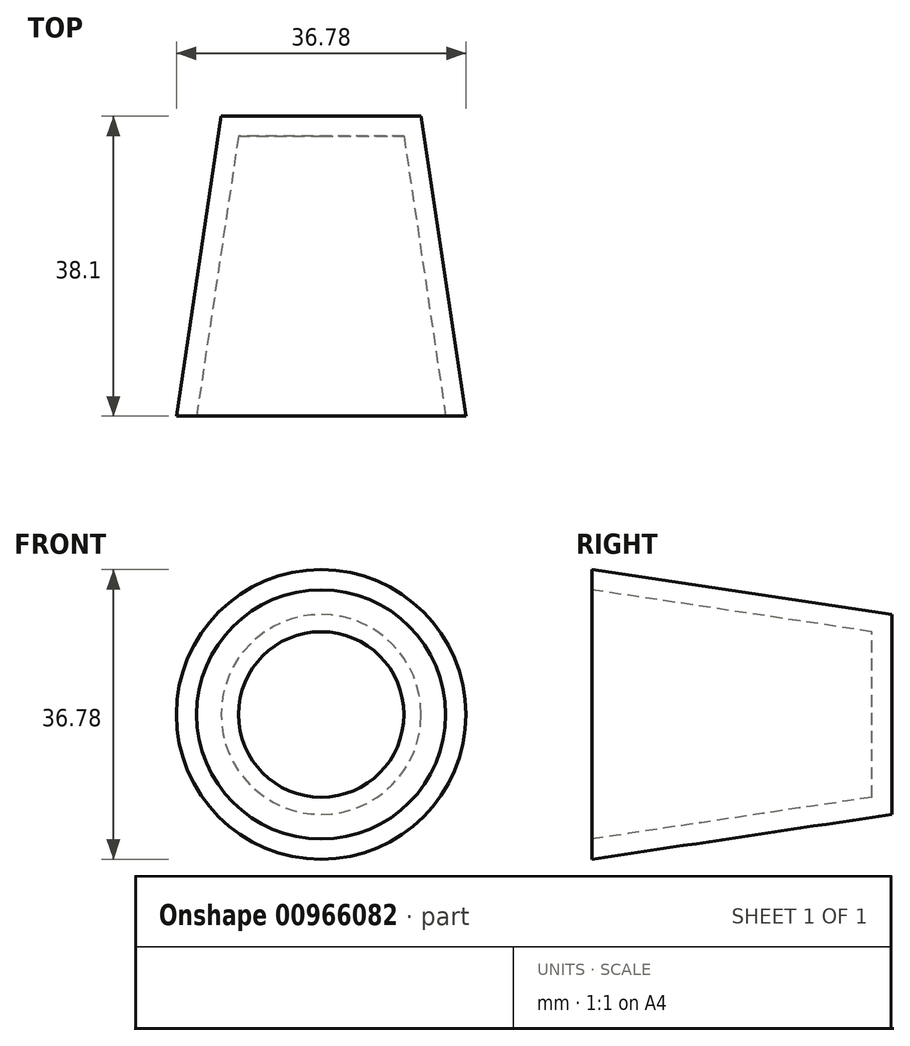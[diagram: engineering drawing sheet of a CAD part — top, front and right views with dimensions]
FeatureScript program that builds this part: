
annotation { "Feature Type Name" : "Feature", "Feature Type Description" : "" }
export const myFeature = defineFeature(function(context is Context, id is Id, definition is map)
    precondition{}
    {
        {
            var Q0;
            Q0=qCreatedBy(makeId("Front.planeOp"),FACE);
            var sketch = newSketch(context, id + "F0", { "sketchPlane" : qUnion([Q0])});
            skCircle(sketch, "E0", {"center": v(0, 0) * mm, "radius": 12.7 * mm});
            skSolve(sketch);
        }
        {
            var Q0;
            Q0 = qSketchRegion(id + "F0", true);
            extrude(context, id + "F1", {"entities" : qUnion([Q0]), "depth" : 38.1 * mm, "offsetDistance" : 25.4 * mm, "hasDraft" : true, "draftAngle" : 8.5 * degree});
        }
        {
            var Q0;
            Q0=makeQuery(id+"F1.opExtrude","CAP_FACE",FACE,{"disambiguationData":[OSD([sQuery(id+"F0.wireOp",EDGE,"E0")])],"isStart":false});
            shell(context, id + "F2", {"entities" : qUnion([Q0]), "thickness" : 2.54 * mm});
        }
    });
